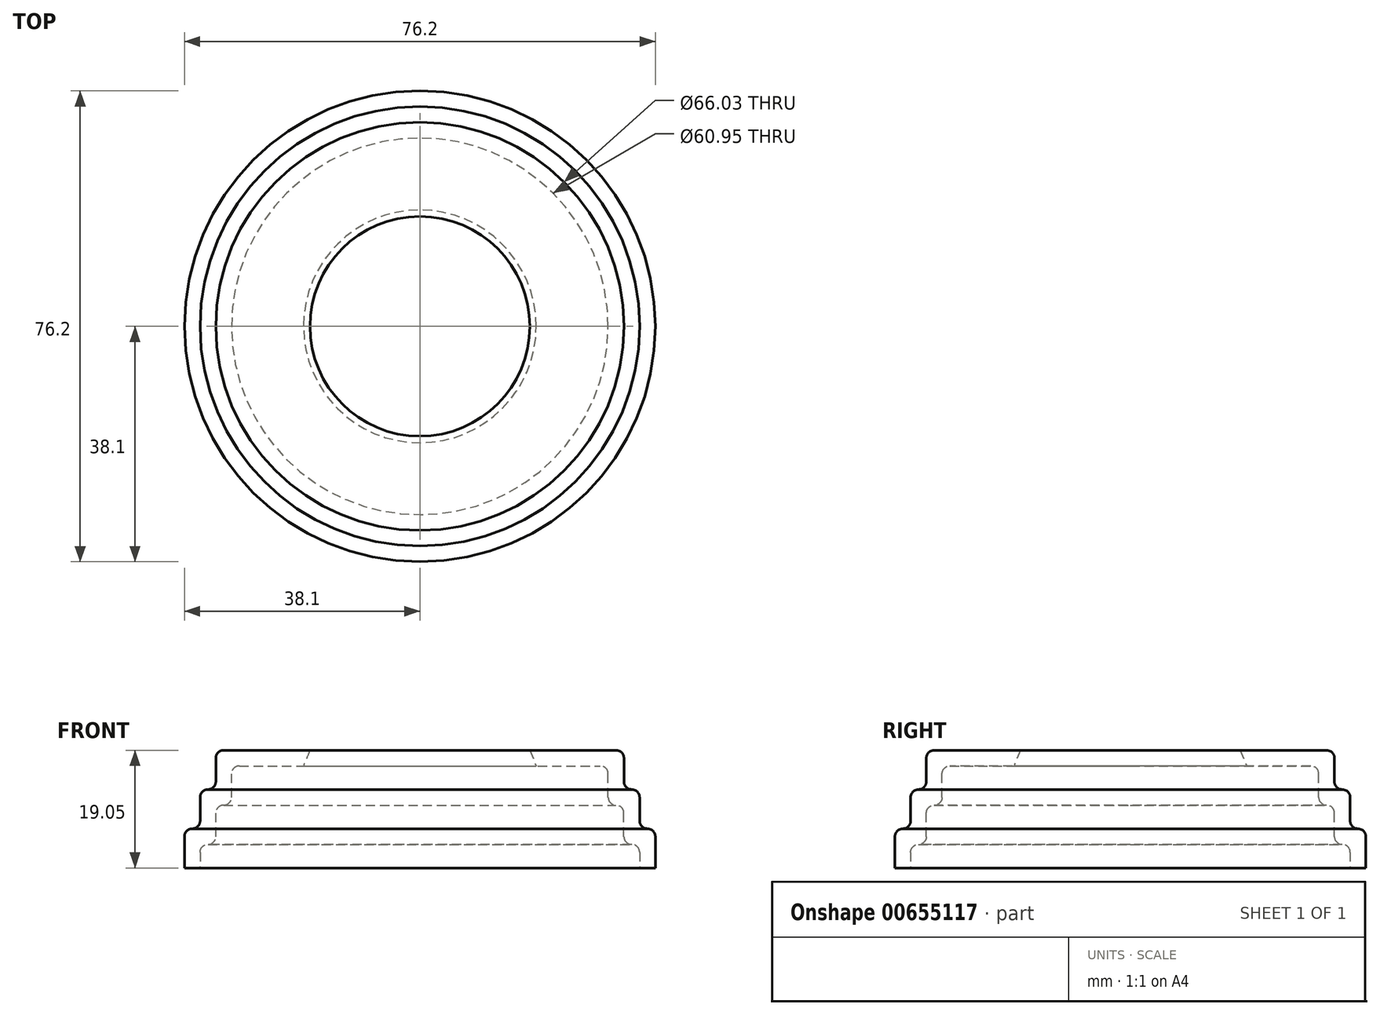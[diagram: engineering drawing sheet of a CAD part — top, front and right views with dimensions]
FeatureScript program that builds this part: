
annotation { "Feature Type Name" : "Feature", "Feature Type Description" : "" }
export const myFeature = defineFeature(function(context is Context, id is Id, definition is map)
    precondition{}
    {
        {
            var Q0;
            Q0=qCreatedBy(makeId("Front.planeOp"),FACE);
            var sketch = newSketch(context, id + "F0", { "sketchPlane" : qUnion([Q0])});
            skLineSegment(sketch, "E0", {"start": v(-38.1, 0) * mm, "end": v(-38.1, 6.35) * mm});
            skLineSegment(sketch, "E1", {"start": v(-38.1, 6.35) * mm, "end": v(-35.56, 6.35) * mm});
            skLineSegment(sketch, "E2", {"start": v(-35.56, 6.35) * mm, "end": v(-35.56, 12.7) * mm});
            skLineSegment(sketch, "E3", {"start": v(-35.56, 12.7) * mm, "end": v(-33.02, 12.7) * mm});
            skLineSegment(sketch, "E4", {"start": v(-33.02, 12.7) * mm, "end": v(-33.02, 19.05) * mm});
            skLineSegment(sketch, "E5", {"start": v(-33.02, 19.05) * mm, "end": v(-12.7, 19.05) * mm});
            skLineSegment(sketch, "E6", {"start": v(-38.1, 0) * mm, "end": v(-35.57, 0) * mm});
            skLineSegment(sketch, "E7", {"start": v(-35.57, 0) * mm, "end": v(-35.56, 3.8) * mm});
            skLineSegment(sketch, "E8", {"start": v(-35.56, 3.8) * mm, "end": v(-33.01, 3.8) * mm});
            skLineSegment(sketch, "E9", {"start": v(-33.01, 3.8) * mm, "end": v(-33.01, 10.16) * mm});
            skLineSegment(sketch, "E10", {"start": v(-33.01, 10.16) * mm, "end": v(-30.47, 10.16) * mm});
            skLineSegment(sketch, "E11", {"start": v(-30.47, 10.16) * mm, "end": v(-30.47, 16.5) * mm});
            skLineSegment(sketch, "E12", {"start": v(-30.47, 16.5) * mm, "end": v(-12.7, 16.5) * mm});
            skLineSegment(sketch, "E13", {"start": v(0, 19.05) * mm, "end": v(0, 0) * mm});
            skLineSegment(sketch, "E14", {"start": v(-12.7, 19.05) * mm, "end": v(-12.7, 16.51) * mm});
            skSolve(sketch);
        }
        {
            var Q0;
            Q0=makeQuery(id+"F0.imprint","IMPRINT",FACE,{"disambiguationData":[TD([[makeQuery(id+"F0.imprint","IMPRINT",EDGE,{"derivedFrom":sQuery(id+"F0.wireOp",EDGE,"E0")}),-1.0]])]});
            var Q1;
            Q1=sQuery(id+"F0.wireOp",EDGE,"E13");
            revolve(context, id + "F1", {"entities" : qUnion([Q0]), "axis" : qUnion([Q1]), "revolveType" : RevolveType.FULL});
        }
        {
            var Q0;
            Q0=makeQuery(id+"F1.opRevolve","SWEPT_EDGE",EDGE,{"disambiguationData":[OSD([sQuery(id+"F0.wireOp",EDGE,"E4"),sQuery(id+"F0.wireOp",EDGE,"E5")])]});
            var Q1;
            Q1=makeQuery(id+"F1.opRevolve","SWEPT_EDGE",EDGE,{"disambiguationData":[OSD([sQuery(id+"F0.wireOp",EDGE,"E2"),sQuery(id+"F0.wireOp",EDGE,"E3")])]});
            var Q2;
            Q2=makeQuery(id+"F1.opRevolve","SWEPT_EDGE",EDGE,{"disambiguationData":[OSD([sQuery(id+"F0.wireOp",EDGE,"E0"),sQuery(id+"F0.wireOp",EDGE,"E1")])]});
            fillet(context, id + "F2", {"entities" : qUnion([Q0, Q1, Q2]), "radius" : 1.27 * mm, "tangentPropagation" : true, "allowEdgeOverflow" : false});
        }
        {
            var Q0;
            Q0=makeQuery(id+"F1.opRevolve","SWEPT_EDGE",EDGE,{"disambiguationData":[OSD([sQuery(id+"F0.wireOp",EDGE,"E1"),sQuery(id+"F0.wireOp",EDGE,"E2")])]});
            var Q1;
            Q1=makeQuery(id+"F1.opRevolve","SWEPT_EDGE",EDGE,{"disambiguationData":[OSD([sQuery(id+"F0.wireOp",EDGE,"E3"),sQuery(id+"F0.wireOp",EDGE,"E4")])]});
            fillet(context, id + "F3", {"entities" : qUnion([Q0, Q1]), "radius" : 1.27 * mm, "tangentPropagation" : true, "allowEdgeOverflow" : false});
        }
        {
            var Q0;
            Q0=makeQuery(id+"F1.opRevolve","SWEPT_EDGE",EDGE,{"disambiguationData":[OSD([sQuery(id+"F0.wireOp",EDGE,"E5"),sQuery(id+"F0.wireOp",EDGE,"E14")])]});
            chamfer(context, id + "F4", {"entities" : qUnion([Q0]), "width" : 2.54 * mm, "tangentPropagation" : true});
        }
        {
            var Q0;
            Q0=makeQuery(id+"F1.opRevolve","SWEPT_EDGE",EDGE,{"disambiguationData":[OSD([sQuery(id+"F0.wireOp",EDGE,"E10"),sQuery(id+"F0.wireOp",EDGE,"E11")])]});
            var Q1;
            Q1=makeQuery(id+"F1.opRevolve","SWEPT_EDGE",EDGE,{"disambiguationData":[OSD([sQuery(id+"F0.wireOp",EDGE,"E8"),sQuery(id+"F0.wireOp",EDGE,"E9")])]});
            fillet(context, id + "F5", {"entities" : qUnion([Q0, Q1]), "radius" : 1.27 * mm, "tangentPropagation" : true, "allowEdgeOverflow" : false});
        }
        {
            var Q0;
            Q0=makeQuery(id+"F1.opRevolve","SWEPT_EDGE",EDGE,{"disambiguationData":[OSD([sQuery(id+"F0.wireOp",EDGE,"E7"),sQuery(id+"F0.wireOp",EDGE,"E8")])]});
            var Q1;
            Q1=makeQuery(id+"F1.opRevolve","SWEPT_EDGE",EDGE,{"disambiguationData":[OSD([sQuery(id+"F0.wireOp",EDGE,"E9"),sQuery(id+"F0.wireOp",EDGE,"E10")])]});
            var Q2;
            Q2=makeQuery(id+"F1.opRevolve","SWEPT_EDGE",EDGE,{"disambiguationData":[OSD([sQuery(id+"F0.wireOp",EDGE,"E11"),sQuery(id+"F0.wireOp",EDGE,"E12")])]});
            fillet(context, id + "F6", {"entities" : qUnion([Q0, Q1, Q2]), "radius" : 1.27 * mm, "tangentPropagation" : true, "allowEdgeOverflow" : false});
        }
        {
            var Q0;
            Q0=makeQuery(id+"F4.opChamfer","BLEND_EDGE",EDGE,{"blendedFrom":[makeQuery(id+"F1.opRevolve","SWEPT_EDGE",EDGE,{"disambiguationData":[OSD([sQuery(id+"F0.wireOp",EDGE,"E5"),sQuery(id+"F0.wireOp",EDGE,"E14")])]}),makeQuery(id+"F1.opRevolve","SWEPT_FACE",FACE,{"disambiguationData":[OSD([sQuery(id+"F0.wireOp",EDGE,"E12")])]})],"blendedInto":[makeQuery(id+"F1.opRevolve","SWEPT_FACE",FACE,{"disambiguationData":[OSD([sQuery(id+"F0.wireOp",EDGE,"E12")])]})]});
            chamfer(context, id + "F7", {"entities" : qUnion([Q0]), "width" : 2.54 * mm, "tangentPropagation" : true});
        }
    });
